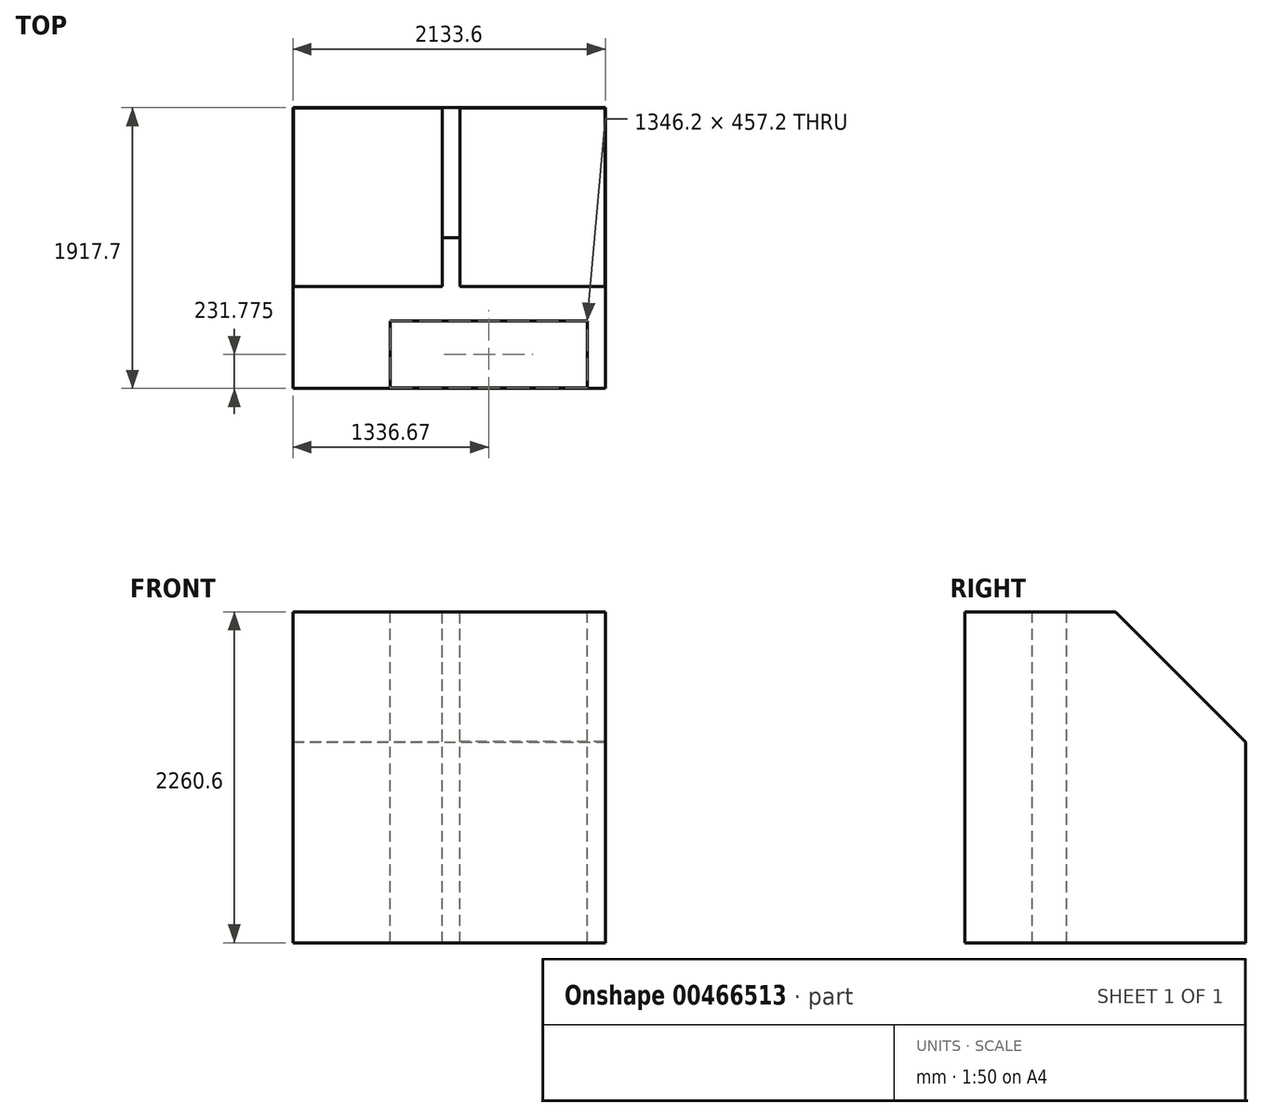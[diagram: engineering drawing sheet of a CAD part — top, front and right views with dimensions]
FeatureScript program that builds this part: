
annotation { "Feature Type Name" : "Feature", "Feature Type Description" : "" }
export const myFeature = defineFeature(function(context is Context, id is Id, definition is map)
    precondition{}
    {
        {
            var Q0;
            Q0=qCreatedBy(makeId("Top.planeOp"),FACE);
            var sketch = newSketch(context, id + "F0", { "sketchPlane" : qUnion([Q0])});
            skLineSegment(sketch, "E0", {"start": v(0, 0) * mm, "end": v(2133.6, 0) * mm});
            skLineSegment(sketch, "E1", {"start": v(2133.6, 0) * mm, "end": v(2133.6, 1917.7) * mm});
            skLineSegment(sketch, "E2", {"start": v(2133.6, 1917.7) * mm, "end": v(0, 1917.7) * mm});
            skLineSegment(sketch, "E3", {"start": v(0, 1917.7) * mm, "end": v(0, 0) * mm});
            skSolve(sketch);
        }
        {
            var Q0;
            Q0 = qSketchRegion(id + "F0", true);
            extrude(context, id + "F1", {"entities" : qUnion([Q0]), "depth" : 2260.6 * mm});
        }
        {
            var Q0;
            Q0=makeQuery(id+"F1.opExtrude","CAP_FACE",FACE,{"disambiguationData":[OSD([sQuery(id+"F0.wireOp",EDGE,"E0"),sQuery(id+"F0.wireOp",EDGE,"E1"),sQuery(id+"F0.wireOp",EDGE,"E2"),sQuery(id+"F0.wireOp",EDGE,"E3")])],"isStart":false});
            var sketch = newSketch(context, id + "F2", { "sketchPlane" : qUnion([Q0])});
            skLineSegment(sketch, "E4.bottom", {"start": v(2130.43, 1914.53) * mm, "end": v(1139.82, 1914.53) * mm});
            skLineSegment(sketch, "E4.top", {"start": v(2130.43, 695.32) * mm, "end": v(1139.83, 695.32) * mm});
            skLineSegment(sketch, "E4.right", {"start": v(1139.82, 1914.53) * mm, "end": v(1139.83, 695.32) * mm});
            skLineSegment(sketch, "E5.bottom", {"start": v(3.18, 1914.52) * mm, "end": v(1019.18, 1914.52) * mm});
            skLineSegment(sketch, "E5.top", {"start": v(3.18, 695.32) * mm, "end": v(1019.18, 695.32) * mm});
            skLineSegment(sketch, "E5.right", {"start": v(1019.18, 1914.53) * mm, "end": v(1019.18, 695.32) * mm});
            skLineSegment(sketch, "E6", {"start": v(3.18, 1914.52) * mm, "end": v(3.18, 695.32) * mm});
            skLineSegment(sketch, "E7", {"start": v(2130.43, 1914.53) * mm, "end": v(2130.43, 695.32) * mm});
            skSolve(sketch);
        }
        {
            var Q0;
            Q0 = qSketchRegion(id + "F2", true);
            extrude(context, id + "F3", {"entities" : qUnion([Q0]), "operationType" : NewBodyOperationType.REMOVE, "endBound" : BoundingType.THROUGH_ALL, "oppositeDirection" : true, "depth" : 25.4 * mm});
        }
        {
            var Q0;
            Q0=makeQuery(id+"F1.opExtrude","CAP_FACE",FACE,{"disambiguationData":[OSD([sQuery(id+"F0.wireOp",EDGE,"E0"),sQuery(id+"F0.wireOp",EDGE,"E1"),sQuery(id+"F0.wireOp",EDGE,"E2"),sQuery(id+"F0.wireOp",EDGE,"E3")])],"isStart":false});
            var sketch = newSketch(context, id + "F4", { "sketchPlane" : qUnion([Q0])});
            skLineSegment(sketch, "E8.bottom", {"start": v(663.58, 460.38) * mm, "end": v(2009.78, 460.38) * mm});
            skLineSegment(sketch, "E8.top", {"start": v(663.58, 3.18) * mm, "end": v(2009.78, 3.18) * mm});
            skLineSegment(sketch, "E8.left", {"start": v(663.58, 460.37) * mm, "end": v(663.58, 3.18) * mm});
            skLineSegment(sketch, "E8.right", {"start": v(2009.78, 460.38) * mm, "end": v(2009.78, 3.18) * mm});
            skLineSegment(sketch, "E9", {"start": v(1019.18, 695.32) * mm, "end": v(1139.83, 695.32) * mm, "construction": true});
            skLineSegment(sketch, "E10", {"start": v(2009.78, 460.38) * mm, "end": v(2130.43, 460.38) * mm, "construction": true});
            skSolve(sketch);
        }
        {
            var Q0;
            Q0 = qSketchRegion(id + "F4", true);
            extrude(context, id + "F5", {"entities" : qUnion([Q0]), "operationType" : NewBodyOperationType.REMOVE, "endBound" : BoundingType.THROUGH_ALL, "oppositeDirection" : true, "depth" : 25.4 * mm});
        }
        {
            var Q0;
            Q0=makeQuery(id+"F1.opExtrude","SWEPT_FACE",FACE,{"disambiguationData":[OSD([sQuery(id+"F0.wireOp",EDGE,"E1")])]});
            var sketch = newSketch(context, id + "F6", { "sketchPlane" : qUnion([Q0])});
            skLineSegment(sketch, "E11", {"start": v(1917.7, 2260.6) * mm, "end": v(1028.7, 2260.6) * mm});
            skLineSegment(sketch, "E12", {"start": v(1028.7, 2260.6) * mm, "end": v(1917.7, 1371.6) * mm});
            skLineSegment(sketch, "E13", {"start": v(1917.7, 1371.6) * mm, "end": v(1917.7, 2260.6) * mm});
            skSolve(sketch);
        }
        {
            var Q0;
            Q0 = qSketchRegion(id + "F6", true);
            extrude(context, id + "F7", {"entities" : qUnion([Q0]), "operationType" : NewBodyOperationType.REMOVE, "endBound" : BoundingType.THROUGH_ALL, "oppositeDirection" : true, "depth" : 25.4 * mm});
        }
    });
